# Revit family: Kawneer - AA3200 IR-Sub Sash (OXO-L) LMI
name_source: partatom
category: Doors
revit_build: Autodesk Revit 2015 (Build: 20140905_0730(x64)
units: mm (PartAtom-declared; Revit-internal decimal feet)

## types (1)
- AA3200 IR-Sub Sash (OXO-L) LMI
    Assembly Code = B2030110
    CSI Masterformat Code = 08 32 13
    Cofigurations = OXO
    Door Panel Height = 6' - 10 1/2"
    Door Panel Width = 3' - 0 1/2"
    Frame Material = Aluminum - 6063-T6 alloy and temper
    Function = Interior
    Glass U-Factor = 0.48
    Glazing Thickness = 0' - 1"
    Height = 7' - 0"
    Manufacturer = Kawneer
    Manufacturer Part Number = AA3200 IR-Sub Sash (OXO-L) LMI
    Overall U-Factor = 0.59
    Panel Inserts Material = Glass
    Product data url = https://bimobject.com
    Sightline = 0' - 0"
    Thickness = 0' - 7"
    URL = http://www.kawneer.com
    Wall Closure = By host
    Width = 9' - 0"

## geometry (parser evidence)
native form markers: Extrusion x5, Sweep x8
no freeform markers — native parametric forms only
